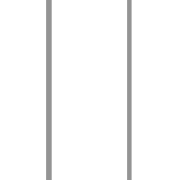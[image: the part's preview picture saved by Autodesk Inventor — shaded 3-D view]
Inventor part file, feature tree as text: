
AUTODESK INVENTOR PART (.ipt)
format: ipt  version: 2021 (Build 250183000, 183)  size: 150,016 bytes
history: native  units: in
note: dims shown in document units (in); Inventor stores cm internally (conversion verified against a paired STEP export)
features: plane x5, sketch x5, other x4, hole x1, extrude x1, boolean_combine x1
ambient origin geometry x8: Origin, YZ Plane, XZ Plane, XY Plane, X Axis, Y Axis, Z Axis, Center Point
bodies: Solid1 (feature_tree), Body (feature_tree), Solid2 (feature_tree)
feature tree (17):
  other  "Driven Length"
  other  "Frame Generator"
  plane  "Work Plane3"
  other  "Start Plane"
  other  "End Plane"
  hole  "Hole2"  [1 undecoded]
  plane  "Work Plane7"
  plane  "Work Plane8"
  plane  "Work Plane9"
  extrude  "Extrusion3"  Depth=0.0625in
  boolean_combine  "Combine1"
  sketch  "Sketch"  dims[d17=2.0in d18=0.12in d19=0.0in d22=1.5in d23=0.4375in d24=0.75in d25=0.635in d26=0.25in d27=0.5635in d28=1.0in d29=0.8108in d32=90.0deg d21=2.0in d34=0.12in d35=0.0in d8=0.5in d9=0.0344in d10=0.5in d11=0.0344in]
  sketch  "Sketch5"  dims[d0=1.5in d1=1.0in]
  sketch  "Sketch8"  dims[d2=0.0625in d3=0.0625in]
  plane  "Work Plane6"
  sketch  "Sketch9"  dims[d4=2.0in]
  sketch  "Sketch10"  dims[d16=-0.0in]
note: 1 required parameter value undecoded (feature->parameter linkage not recoverable at this tier; creation-order binding heuristic only, values carry confidence <= 0.55)
